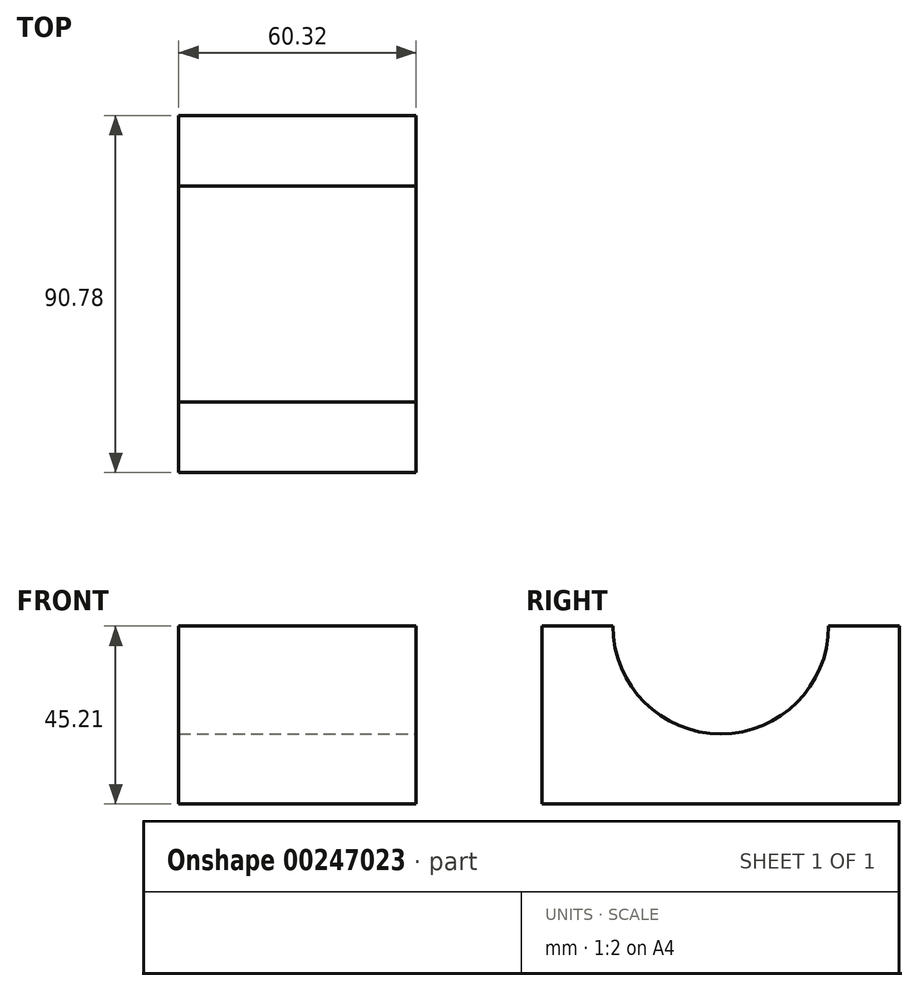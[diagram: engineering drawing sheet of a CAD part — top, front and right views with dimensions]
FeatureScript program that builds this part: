
annotation { "Feature Type Name" : "Feature", "Feature Type Description" : "" }
export const myFeature = defineFeature(function(context is Context, id is Id, definition is map)
    precondition{}
    {
        {
            var Q0;
            Q0=qCreatedBy(makeId("Top.planeOp"),FACE);
            var sketch = newSketch(context, id + "F0", { "sketchPlane" : qUnion([Q0])});
            skLineSegment(sketch, "E0.bottom", {"start": v(-30.16, 45.4) * mm, "end": v(30.16, 45.4) * mm});
            skLineSegment(sketch, "E0.top", {"start": v(-30.16, -45.4) * mm, "end": v(30.16, -45.4) * mm});
            skLineSegment(sketch, "E0.left", {"start": v(-30.16, 45.4) * mm, "end": v(-30.16, -45.4) * mm});
            skLineSegment(sketch, "E0.right", {"start": v(30.16, 45.4) * mm, "end": v(30.16, -45.4) * mm});
            skPoint(sketch, "E0.middle", {"position": v(0, 0) * mm});
            skSolve(sketch);
        }
        {
            var Q0;
            Q0=makeQuery(id+"F0.imprint","IMPRINT",FACE,{"disambiguationData":[TD([[makeQuery(id+"F0.imprint","IMPRINT",EDGE,{"derivedFrom":sQuery(id+"F0.wireOp",EDGE,"E0.bottom")}),-1.0]])]});
            extrude(context, id + "F1", {"entities" : qUnion([Q0]), "depth" : 45.2 * mm});
        }
        {
            var Q0;
            Q0=makeQuery(id+"F1.opExtrude","SWEPT_FACE",FACE,{"disambiguationData":[OSD([sQuery(id+"F0.wireOp",EDGE,"E0.right")])]});
            var sketch = newSketch(context, id + "F2", { "sketchPlane" : qUnion([Q0])});
            skCircle(sketch, "E1", {"center": v(0, 45.21) * mm, "radius": 27.38 * mm});
            skSolve(sketch);
        }
        {
            var Q0;
            {var subQ0=sQuery(id+"F2.wireOp",EDGE,"E1");var subQ1=makeQuery(id+"F1.opExtrude","CAP_EDGE",EDGE,{"disambiguationData":[OSD([sQuery(id+"F0.wireOp",EDGE,"E0.right")])],"isStart":false});var subQ2=makeQuery(id+"F2.imprint","INTERSECT",VERTEX,{"disambiguationData":[OD(0.0)],"derivedFrom":[subQ1,subQ0]});Q0=makeQuery(id+"F2.imprint","IMPRINT",FACE,{"disambiguationData":[TD([[makeQuery(id+"F2.imprint","IMPRINT",EDGE,{"disambiguationData":[TD([[subQ2,1.0]])],"derivedFrom":subQ0}),1.0]])]});}
            var Q1;
            {var subQ0=sQuery(id+"F2.wireOp",EDGE,"E1");var subQ1=makeQuery(id+"F1.opExtrude","CAP_EDGE",EDGE,{"disambiguationData":[OSD([sQuery(id+"F0.wireOp",EDGE,"E0.right")])],"isStart":false});var subQ2=makeQuery(id+"F2.imprint","INTERSECT",VERTEX,{"disambiguationData":[OD(0.0)],"derivedFrom":[subQ1,subQ0]});Q1=makeQuery(id+"F2.imprint","IMPRINT",FACE,{"disambiguationData":[TD([[makeQuery(id+"F2.imprint","IMPRINT",EDGE,{"disambiguationData":[TD([[subQ2,-1.0]])],"derivedFrom":subQ0}),1.0]])]});}
            extrude(context, id + "F3", {"entities" : qUnion([Q0, Q1]), "operationType" : NewBodyOperationType.REMOVE, "oppositeDirection" : true, "depth" : 80.26 * mm});
        }
    });
